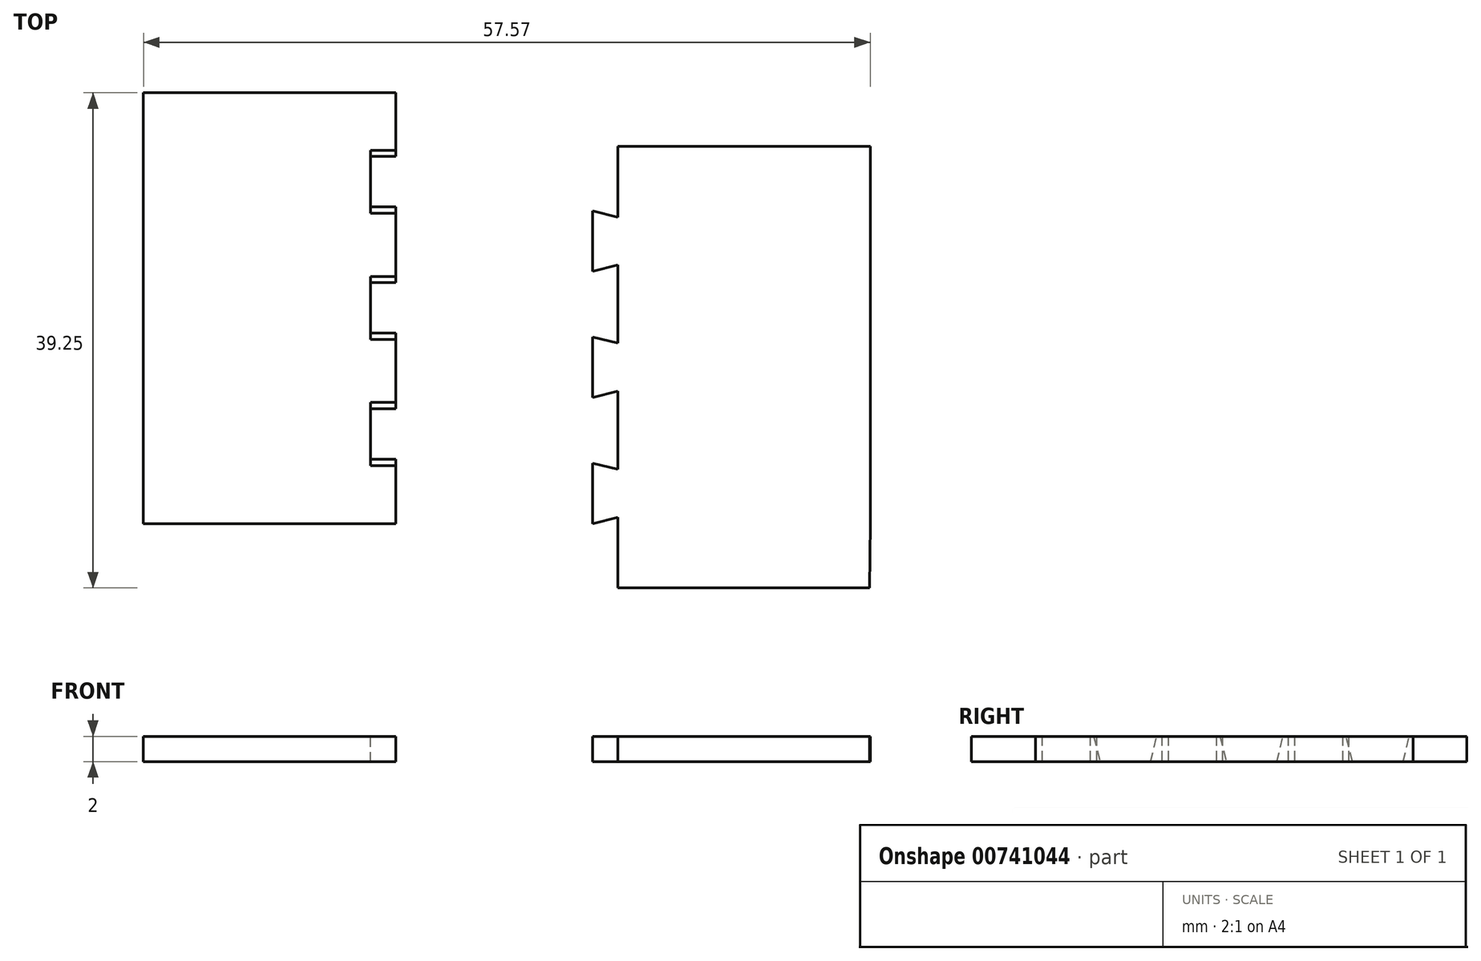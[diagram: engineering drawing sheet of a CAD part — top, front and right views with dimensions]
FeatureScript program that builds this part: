
annotation { "Feature Type Name" : "Feature", "Feature Type Description" : "" }
export const myFeature = defineFeature(function(context is Context, id is Id, definition is map)
    precondition{}
    {
        {
            var Q0;
            Q0=qCreatedBy(makeId("Top.planeOp"),FACE);
            var sketch = newSketch(context, id + "F0", { "sketchPlane" : qUnion([Q0])});
            skLineSegment(sketch, "E0.bottom", {"start": v(-27.38, 34.15) * mm, "end": v(-7.38, 34.15) * mm});
            skLineSegment(sketch, "E0.top", {"start": v(-27.38, 0) * mm, "end": v(-7.38, 0) * mm});
            skLineSegment(sketch, "E0.left", {"start": v(-27.38, 34.15) * mm, "end": v(-27.38, 0) * mm});
            skLineSegment(sketch, "E0.right", {"start": v(-7.38, 34.15) * mm, "end": v(-7.38, 29.1) * mm});
            skLineSegment(sketch, "E1.bottom", {"start": v(10.19, 29.9) * mm, "end": v(30.19, 29.9) * mm});
            skLineSegment(sketch, "E1.left", {"start": v(10.19, 29.9) * mm, "end": v(10.19, 24.8) * mm});
            skLineSegment(sketch, "E1.right", {"start": v(30.19, 29.9) * mm, "end": v(30.19, 0) * mm});
            skLineSegment(sketch, "E2.bottom", {"start": v(-9.38, 29.1) * mm, "end": v(-7.38, 29.1) * mm});
            skLineSegment(sketch, "E2.top", {"start": v(-9.38, 25.1) * mm, "end": v(-7.38, 25.1) * mm});
            skLineSegment(sketch, "E2.left", {"start": v(-9.38, 29.1) * mm, "end": v(-9.38, 25.1) * mm});
            skLineSegment(sketch, "E3.bottom", {"start": v(-9.38, 19.1) * mm, "end": v(-7.38, 19.1) * mm});
            skLineSegment(sketch, "E3.top", {"start": v(-9.38, 15.1) * mm, "end": v(-7.38, 15.1) * mm});
            skLineSegment(sketch, "E3.left", {"start": v(-9.38, 19.1) * mm, "end": v(-9.38, 15.1) * mm});
            skLineSegment(sketch, "E4.bottom", {"start": v(-9.38, 9.1) * mm, "end": v(-7.38, 9.1) * mm});
            skLineSegment(sketch, "E4.top", {"start": v(-9.38, 5.1) * mm, "end": v(-7.38, 5.1) * mm});
            skLineSegment(sketch, "E4.left", {"start": v(-9.38, 9.1) * mm, "end": v(-9.38, 5.1) * mm});
            skLineSegment(sketch, "E5.left", {"start": v(8.19, 24.8) * mm, "end": v(8.19, 20) * mm});
            skLineSegment(sketch, "E6.left", {"start": v(8.19, 14.8) * mm, "end": v(8.19, 10) * mm});
            skLineSegment(sketch, "E7.left", {"start": v(8.19, 4.8) * mm, "end": v(8.19, 0) * mm});
            skLineSegment(sketch, "E8.trimOffspring", {"start": v(-7.38, 25.1) * mm, "end": v(-7.38, 19.1) * mm});
            skLineSegment(sketch, "E9.trimOffspring", {"start": v(-7.38, 15.1) * mm, "end": v(-7.38, 9.1) * mm});
            skLineSegment(sketch, "E10.trimOffspring", {"start": v(-7.38, 5.1) * mm, "end": v(-7.38, 0) * mm});
            skLineSegment(sketch, "E11.trimOffspring", {"start": v(10.19, 10) * mm, "end": v(10.19, 4.8) * mm});
            skLineSegment(sketch, "E12.trimOffspring", {"start": v(10.19, 20) * mm, "end": v(10.19, 14.8) * mm});
            skLineSegment(sketch, "E13.top", {"start": v(10.19, -5.1) * mm, "end": v(30.13, -5.1) * mm});
            skLineSegment(sketch, "E13.left", {"start": v(10.19, 0) * mm, "end": v(10.19, -5.1) * mm});
            skLineSegment(sketch, "E14.trimOffspring", {"start": v(30.13, 0) * mm, "end": v(30.19, 0) * mm});
            skLineSegment(sketch, "E15", {"start": v(30.19, 0) * mm, "end": v(30.13, -5.1) * mm});
            skLineSegment(sketch, "E16", {"start": v(8.19, 20) * mm, "end": v(10.19, 20.5) * mm});
            skLineSegment(sketch, "E17", {"start": v(10.19, 20.5) * mm, "end": v(10.19, 24.3) * mm});
            skLineSegment(sketch, "E18", {"start": v(10.19, 24.3) * mm, "end": v(8.19, 24.8) * mm});
            skLineSegment(sketch, "E19", {"start": v(10.19, 24.8) * mm, "end": v(10.19, 24.3) * mm});
            skLineSegment(sketch, "E20", {"start": v(10.19, 20.5) * mm, "end": v(10.19, 20) * mm});
            skLineSegment(sketch, "E21", {"start": v(8.19, 14.8) * mm, "end": v(10.19, 14.3) * mm});
            skLineSegment(sketch, "E22", {"start": v(10.19, 14.3) * mm, "end": v(10.19, 10.5) * mm});
            skLineSegment(sketch, "E23", {"start": v(10.19, 10.5) * mm, "end": v(8.19, 10) * mm});
            skLineSegment(sketch, "E24", {"start": v(10.19, 10.5) * mm, "end": v(10.19, 10) * mm});
            skLineSegment(sketch, "E25", {"start": v(10.19, 14.8) * mm, "end": v(10.19, 14.3) * mm});
            skLineSegment(sketch, "E26", {"start": v(8.19, 4.8) * mm, "end": v(10.19, 4.3) * mm});
            skLineSegment(sketch, "E27", {"start": v(10.19, 4.3) * mm, "end": v(10.19, 0.5) * mm});
            skLineSegment(sketch, "E28", {"start": v(10.19, 0.5) * mm, "end": v(8.19, 0) * mm});
            skLineSegment(sketch, "E29", {"start": v(10.19, 4.3) * mm, "end": v(10.19, 4.8) * mm});
            skLineSegment(sketch, "E30", {"start": v(10.19, 0) * mm, "end": v(10.19, 0.5) * mm});
            skLineSegment(sketch, "E31", {"start": v(10.19, 10) * mm, "end": v(8.19, 10) * mm, "construction": true});
            skLineSegment(sketch, "E32", {"start": v(10.19, 14.8) * mm, "end": v(8.19, 14.8) * mm, "construction": true});
            skLineSegment(sketch, "E33", {"start": v(10.19, 4.8) * mm, "end": v(8.19, 4.8) * mm, "construction": true});
            skLineSegment(sketch, "E34", {"start": v(10.19, 0) * mm, "end": v(8.19, 0) * mm, "construction": true});
            skLineSegment(sketch, "E35", {"start": v(10.19, 20) * mm, "end": v(8.19, 20) * mm, "construction": true});
            skLineSegment(sketch, "E36", {"start": v(10.19, 24.8) * mm, "end": v(8.19, 24.8) * mm, "construction": true});
            skSolve(sketch);
        }
        {
            var Q0;
            Q0 = qSketchRegion(id + "F0", true);
            extrude(context, id + "F1", {"entities" : qUnion([Q0]), "depth" : 2 * mm, "offsetDistance" : 25 * mm});
        }
        {
            var Q0;
            Q0=makeQuery(id+"F1.opExtrude","CAP_EDGE",EDGE,{"disambiguationData":[OSD([sQuery(id+"F0.wireOp",EDGE,"E2.bottom")])],"isStart":false});
            var Q1;
            Q1=makeQuery(id+"F1.opExtrude","CAP_EDGE",EDGE,{"disambiguationData":[OSD([sQuery(id+"F0.wireOp",EDGE,"E2.top")])],"isStart":false});
            var Q2;
            Q2=makeQuery(id+"F1.opExtrude","CAP_EDGE",EDGE,{"disambiguationData":[OSD([sQuery(id+"F0.wireOp",EDGE,"E3.bottom")])],"isStart":false});
            var Q3;
            Q3=makeQuery(id+"F1.opExtrude","CAP_EDGE",EDGE,{"disambiguationData":[OSD([sQuery(id+"F0.wireOp",EDGE,"E3.top")])],"isStart":false});
            var Q4;
            Q4=makeQuery(id+"F1.opExtrude","CAP_EDGE",EDGE,{"disambiguationData":[OSD([sQuery(id+"F0.wireOp",EDGE,"E4.bottom")])],"isStart":false});
            var Q5;
            Q5=makeQuery(id+"F1.opExtrude","CAP_EDGE",EDGE,{"disambiguationData":[OSD([sQuery(id+"F0.wireOp",EDGE,"E4.top")])],"isStart":false});
            chamfer(context, id + "F2", {"entities" : qUnion([Q0, Q1, Q2, Q3, Q4, Q5]), "chamferType" : ChamferType.OFFSET_ANGLE, "width" : 0.5 * mm, "oppositeDirection" : false, "angle" : 75.96 * degree, "tangentPropagation" : true});
        }
    });
